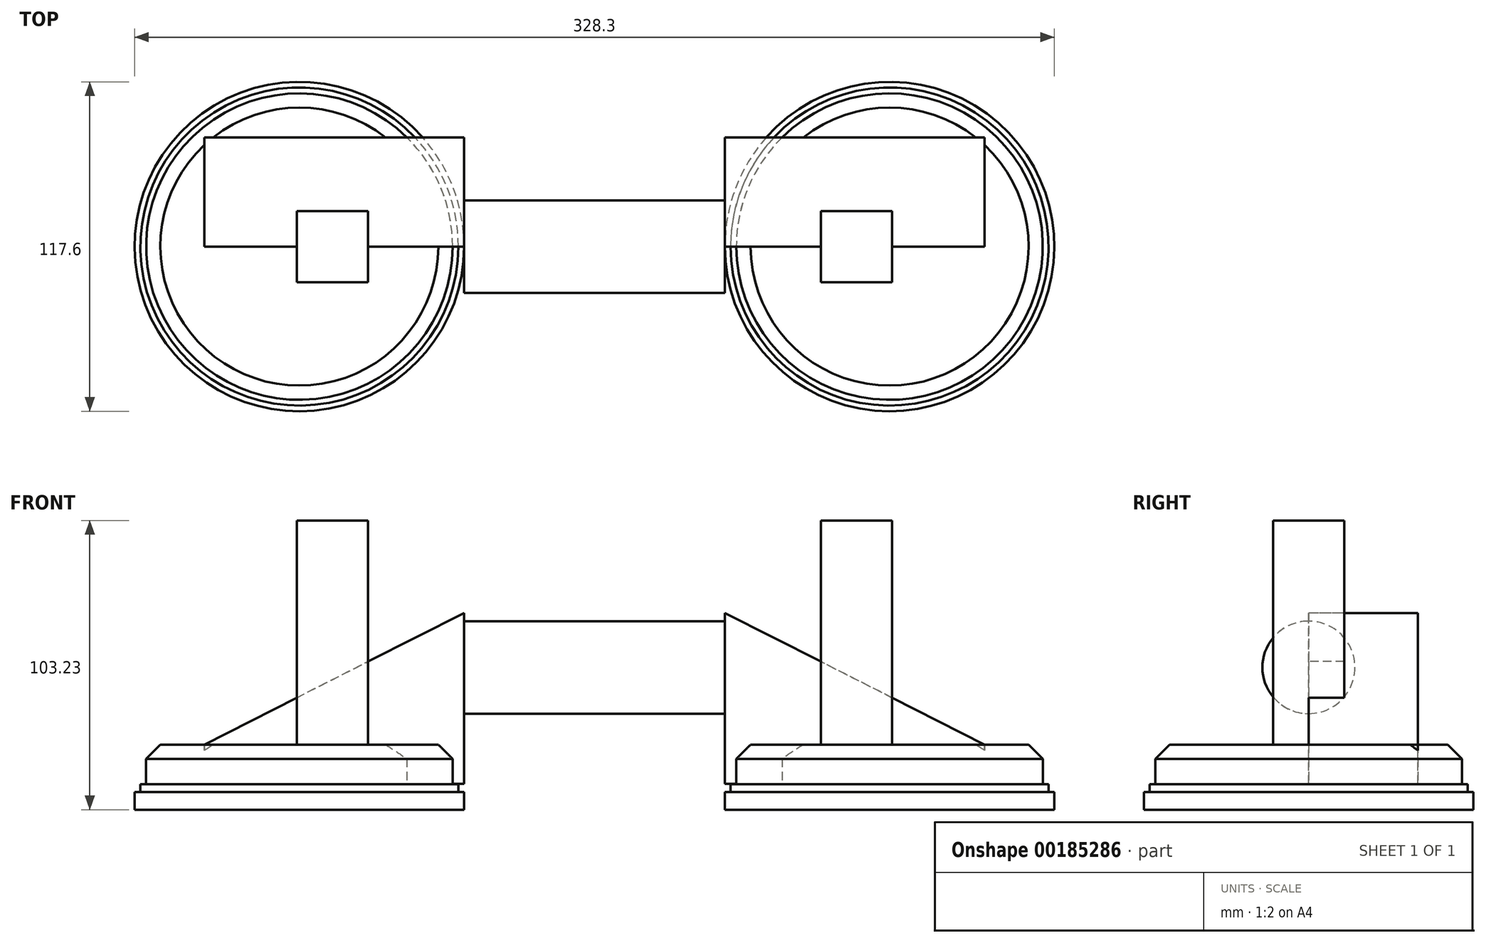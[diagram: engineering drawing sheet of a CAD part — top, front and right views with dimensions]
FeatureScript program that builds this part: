
annotation { "Feature Type Name" : "Feature", "Feature Type Description" : "" }
export const myFeature = defineFeature(function(context is Context, id is Id, definition is map)
    precondition{}
    {
        {
            var Q0;
            Q0=qCreatedBy(makeId("Top.planeOp"),FACE);
            var sketch = newSketch(context, id + "F0", { "sketchPlane" : qUnion([Q0])});
            skCircle(sketch, "E0", {"center": v(-105.35, 0) * mm, "radius": 58.8 * mm});
            skLineSegment(sketch, "E1", {"start": v(0, 0) * mm, "end": v(0, 0) * mm});
            skLineSegment(sketch, "E2", {"start": v(-164.15, 0) * mm, "end": v(-164.15, 52.4) * mm, "construction": true});
            skLineSegment(sketch, "E3", {"start": v(0, 0) * mm, "end": v(0, 54.26) * mm, "construction": true});
            skLineSegment(sketch, "E4", {"start": v(-46.55, 0) * mm, "end": v(-46.55, 54.05) * mm, "construction": true});
            skSolve(sketch);
        }
        {
            var Q0;
            Q0 = qSketchRegion(id + "F0", true);
            extrude(context, id + "F1", {"entities" : qUnion([Q0]), "depth" : 6.35 * mm});
        }
        {
            var Q0;
            Q0=qCreatedBy(makeId("Front.planeOp"),FACE);
            cPlane(context, id + "F2", {"entities" : qUnion([Q0]), "cplaneType" : CPlaneType.OFFSET, "offset" : 1.53 / 50.8 * mm, "width" : 152.4 * mm, "height" : 152.4 * mm});
        }
        {
            var Q0;
            Q0=makeQuery(id+"F1.opExtrude","CAP_FACE",FACE,{"disambiguationData":[OSD([sQuery(id+"F0.wireOp",EDGE,"E0")])],"isStart":false});
            var sketch = newSketch(context, id + "F3", { "sketchPlane" : qUnion([Q0])});
            skCircle(sketch, "E5", {"center": v(-105.35, 0) * mm, "radius": 56.77 * mm});
            skSolve(sketch);
        }
        {
            var Q0;
            Q0 = qSketchRegion(id + "F3", true);
            extrude(context, id + "F4", {"entities" : qUnion([Q0]), "operationType" : NewBodyOperationType.ADD, "depth" : 2.8 * mm});
        }
        {
            var Q0;
            Q0=makeQuery(id+"F4.opExtrude","CAP_FACE",FACE,{"disambiguationData":[OSD([sQuery(id+"F3.wireOp",EDGE,"E5")])],"isStart":false});
            var sketch = newSketch(context, id + "F5", { "sketchPlane" : qUnion([Q0])});
            skCircle(sketch, "E6", {"center": v(-105.35, 0) * mm, "radius": 54.7 * mm});
            skSolve(sketch);
        }
        {
            var Q0;
            Q0=makeQuery(id+"F5.imprint","IMPRINT",FACE,{"disambiguationData":[TD([[makeQuery(id+"F5.imprint","IMPRINT",EDGE,{"derivedFrom":sQuery(id+"F5.wireOp",EDGE,"E6")}),1.0]])]});
            extrude(context, id + "F6", {"entities" : qUnion([Q0]), "operationType" : NewBodyOperationType.ADD, "depth" : 14.07 * mm});
        }
        {
            var Q0;
            Q0=makeQuery(id+"F6.opExtrude","CAP_EDGE",EDGE,{"disambiguationData":[OSD([sQuery(id+"F5.wireOp",EDGE,"E6")])],"isStart":false});
            chamfer(context, id + "F7", {"entities" : qUnion([Q0]), "width" : 5.08 * mm, "tangentPropagation" : true});
        }
        {
            var Q0;
            Q0=qCreatedBy(id+"F2.planeOp",FACE);
            var sketch = newSketch(context, id + "F8", { "sketchPlane" : qUnion([Q0])});
            skLineSegment(sketch, "E7", {"start": v(-46.55, 9.27) * mm, "end": v(-46.55, 70.23) * mm});
            skLineSegment(sketch, "E8", {"start": v(-46.55, 70.23) * mm, "end": v(-139.26, 23.24) * mm});
            skLineSegment(sketch, "E9", {"start": v(-139.26, 23.24) * mm, "end": v(-139.26, 9.27) * mm});
            skLineSegment(sketch, "E10", {"start": v(-139.26, 9.27) * mm, "end": v(-46.55, 9.27) * mm});
            skSolve(sketch);
        }
        {
            var Q0;
            Q0=makeQuery(id+"F8.imprint","IMPRINT",FACE,{"disambiguationData":[TD([[makeQuery(id+"F8.imprint","IMPRINT",EDGE,{"derivedFrom":sQuery(id+"F8.wireOp",EDGE,"E7")}),1.0]])]});
            extrude(context, id + "F9", {"entities" : qUnion([Q0]), "operationType" : NewBodyOperationType.ADD, "oppositeDirection" : true, "offsetDistance" : 25.4 * mm, "depth" : 39 * mm});
        }
        {
            var Q0;
            Q0=qCreatedBy(makeId("Right.planeOp"),FACE);
            var sketch = newSketch(context, id + "F10", { "sketchPlane" : qUnion([Q0])});
            skCircle(sketch, "E11", {"center": v(0, 50.8) * mm, "radius": 16.51 * mm});
            skSolve(sketch);
        }
        {
            var Q0;
            Q0=makeQuery(id+"F10.imprint","IMPRINT",FACE,{"disambiguationData":[TD([[makeQuery(id+"F10.imprint","IMPRINT",EDGE,{"derivedFrom":sQuery(id+"F10.wireOp",EDGE,"E11")}),1.0]])]});
            var Q1;
            Q1=makeQuery(id+"F9.opExtrude","SWEPT_FACE",FACE,{"disambiguationData":[OSD([sQuery(id+"F8.wireOp",EDGE,"E7")])]});
            extrude(context, id + "F11", {"entities" : qUnion([Q0]), "operationType" : NewBodyOperationType.ADD, "endBound" : BoundingType.UP_TO_SURFACE, "oppositeDirection" : true, "endBoundEntityFace" : qUnion([Q1]), "offsetDistance" : 25.4 * mm, "depth" : 25.4 * mm});
        }
        {
            var Q0;
            Q0=qCreatedBy(makeId("Front.planeOp"),FACE);
            var sketch = newSketch(context, id + "F12", { "sketchPlane" : qUnion([Q0])});
            skLineSegment(sketch, "E12", {"start": v(-46.55, 23.22) * mm, "end": v(-106.24, 23.22) * mm, "construction": true});
            skLineSegment(sketch, "E13.bottom", {"start": v(-106.24, 23.22) * mm, "end": v(-80.84, 23.22) * mm});
            skLineSegment(sketch, "E14.top", {"start": v(-106.24, 103.23) * mm, "end": v(-80.84, 103.23) * mm});
            skLineSegment(sketch, "E14.left", {"start": v(-106.24, 23.22) * mm, "end": v(-106.24, 103.23) * mm});
            skLineSegment(sketch, "E14.right", {"start": v(-80.84, 23.22) * mm, "end": v(-80.84, 103.23) * mm});
            skSolve(sketch);
        }
        {
            var Q0;
            Q0 = qSketchRegion(id + "F12", true);
            extrude(context, id + "F13", {"entities" : qUnion([Q0]), "operationType" : NewBodyOperationType.ADD, "endBound" : BoundingType.SYMMETRIC, "depth" : 25.4 * mm});
        }
        {
            var Q0;
            Q0=makeQuery(id+"F1.opExtrude","SWEPT_BODY",BODY,{"disambiguationData":[OSD([sQuery(id+"F0.wireOp",EDGE,"E0")])]});
            var Q1;
            Q1=qCreatedBy(makeId("Right.planeOp"),FACE);
            mirror(context, id + "F14", {"operationType" : NewBodyOperationType.ADD, "entities" : qUnion([Q0]), "mirrorPlane" : qUnion([Q1])});
        }
    });
